# Revit family: NLRS_50_ME_UN_AV_Technea Shower HR-1-21_ARCH
name_source: partatom
category: Mechanical Equipment
units: mm (PartAtom-declared; Revit-internal decimal feet)

## family parameters
Always vertical = Yes
Cut with Voids When Loaded = Yes
Part Type = Normal
Room Calculation Point = No
Round Connector Dimension = Use Diameter
Shared = No
Work Plane-Based = No

## types (1)
- Shower HR 1-21
    Description = dwtw afvoer
    IfcDescription = dwtw afvoer
    IfcExportAs = IfcHeatExchangerType
    IfcExportType = USERDEFINED
    Manufacturer = Technea
    Model = Shower HR 1-21
    NLRS_C_code_STABU = 50
    NLRS_C_code_SfB_tabel1 = 52
    NLRS_C_hoogte = 2100 mm  [stored 6.88976 ft]
    NLRS_C_leverancier_bedrijfsnaam = Technea
    NLRS_C_niveau ontwikkeling = LOD 400
    NLRS_P_c01_aansluitmethode = Lijmmof Ø50mm
    NLRS_P_c02_aansluitmethode = koutwater aansluiting 3/4 buitendraad BSP
    NLRS_P_c03_aansluitmethode = verwarmde wateraansluiting naar thermostaatkraan
    RSen_C_code_manufacturer_gln = -
    RSen_C_content_version = 1.0
    aansluitnippels_hoh = 2002 mm  [stored 6.56824 ft]

note: [stored X ft] marks values corroborated as IEEE doubles in the binary element streams (Revit-internal decimal feet)

## geometry (parser evidence)
native form markers: Sweep x23
no freeform markers — native parametric forms only
